# Revit family: Gira_057000
name_source: partatom
category: Generic Models
revit_build: Autodesk Revit 2017 (Build: 20160225_1515(x64)
units: mm (PartAtom-declared; Revit-internal decimal feet)

## family parameters
Can host rebar = No
Cut with Voids When Loaded = No
Host = Face
Part Type = Normal
Room Calculation Point = No
Round Connector Dimension = Use Diameter
Shared = No

## types (1)
- Bus coup. KNX insert
    BIM = https://media.live.bim.site
    BIMSITE_PRODUCT_ID = bc3e54458c7a90461a68c8f00fad60ed08584449
    Cost = 0 $
    Default Elevation = 1219 mm
    Description = Ins.bus coup. KNX Insert for KNX bus coupler, Features: - The bus coupler is the interface between the bus and the KNX application module, such as an Info Display, data interface RS232, or automatic control switch. - The bus coupler can receive, send, and evaluate messages. - The bus coupler contains the address, the system program, and user-specific programs. - Programming the physical address is authorised by pressing the programming button. - Status display via red programming LED.,Notes : - For device box with screw attachment only.
    GTIN = 4010337570004
    HAN = 057000
    HeinzeBIM = https://www.heinze.de
    Manufacturer = Gira
    Type of fastening = Mounting with claw and screw
    URL = https://www.gira.de

## geometry (parser evidence)
native form markers: Blend x2, Sweep x3
no freeform markers — native parametric forms only
